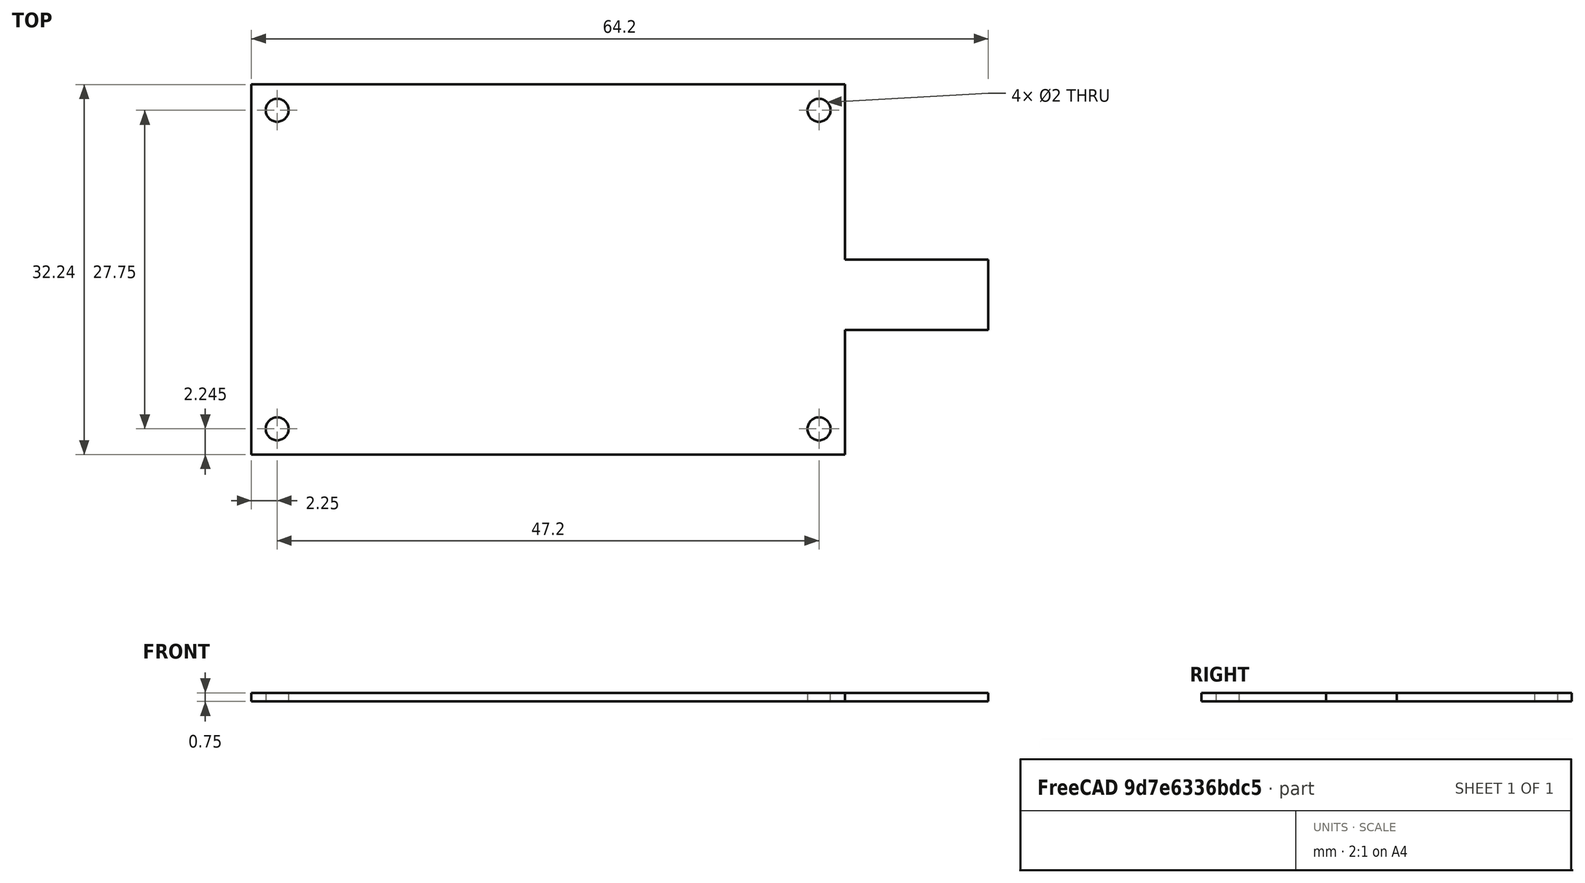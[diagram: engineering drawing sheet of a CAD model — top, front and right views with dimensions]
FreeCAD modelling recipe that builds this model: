
FCSTD DOCUMENT  (FreeCAD 1.0R39109 (Git))
Label: LightAPRS1
License: Creative Commons Attribution-ShareAlike 4.0
LicenseURL: https://creativecommons.org/licenses/by-sa/4.0/
objects: Sketcher::SketchObject×1, PartDesign::Pad×1, PartDesign::Body×1
note: 6 computed .brp shape members not serialized (recipe doc carries the construction recipe); baked Part::Feature solids carry a one-line shape summary decoded from their .brp

FEATURE [Sketcher::SketchObject] Sketch
  ArcFitTolerance = 1e-06
  AttachmentSupport = -> [XY_Plane]
  FullyConstrained = true
  MakeInternals = false
  MapMode = 5
  sketch-geometry (12):
    g0: LineSegment StartX=-25.85 StartY=16.125 StartZ=0 EndX=25.85 EndY=16.125 EndZ=0
    g1: LineSegment StartX=25.85 StartY=16.125 StartZ=0 EndX=25.85 EndY=0.875 EndZ=0
    g2: LineSegment StartX=25.85 StartY=0.875 StartZ=0 EndX=38.35 EndY=0.875 EndZ=0
    g3: LineSegment StartX=38.35 StartY=0.875 StartZ=0 EndX=38.35 EndY=-5.275 EndZ=0
    g4: LineSegment StartX=38.35 StartY=-5.275 StartZ=0 EndX=25.85 EndY=-5.275 EndZ=0
    g5: LineSegment StartX=25.85 StartY=-5.275 StartZ=0 EndX=25.85 EndY=-16.125 EndZ=0
    g6: LineSegment StartX=25.85 StartY=-16.125 StartZ=0 EndX=-25.85 EndY=-16.125 EndZ=0
    g7: LineSegment StartX=-25.85 StartY=-16.125 StartZ=0 EndX=-25.85 EndY=16.125 EndZ=0
    g8: Circle CenterX=-23.6 CenterY=13.875 CenterZ=0 NormalX=0 NormalY=0 NormalZ=1 AngleXU=0 Radius=1
    g9: Circle CenterX=23.6 CenterY=-13.875 CenterZ=0 NormalX=0 NormalY=0 NormalZ=1 AngleXU=0 Radius=1
    g10: Circle CenterX=23.6 CenterY=13.875 CenterZ=0 NormalX=0 NormalY=0 NormalZ=1 AngleXU=0 Radius=1
    g11: Circle CenterX=-23.6 CenterY=-13.875 CenterZ=0 NormalX=0 NormalY=0 NormalZ=1 AngleXU=0 Radius=1
  constraints (35):
    c: Horizontal(g0)
    c: Coincident(g0,g1)
    c: Vertical(g1)
    c: Coincident(g1,g2)
    c: Horizontal(g2)
    c: Coincident(g2,g3)
    c: Vertical(g3)
    c: Coincident(g3,g4)
    c: Horizontal(g4)
    c: Coincident(g4,g5)
    c: Vertical(g5)
    c: Coincident(g5,g6)
    c: Horizontal(g6)
    c: Coincident(g6,g7)
    c: Coincident(g7,g0)
    c: Vertical(g7)
    c: DistanceY(g6,g0) = 32.25
    c: Distance(g0,g1) = 51.7
    c: Vertical(g0,g5)
    c: Distance(g2,g3) = 6.15
    c: DistanceY(g1,g0) = 15.25
    c: Distance(g1,g2) = 12.5
    c: Symmetric(g0,g5,g-1)
    c: Diameter(g8) = 2
    c: Distance(g8,g7) = 2.25
    c: Distance(g8,g0) = 2.25
    c: Equal(g8,g10)
    c: Equal(g10,g9)
    c: Equal(g9,g11)
    c: Distance(g10,g1) = 2.25
    c: Distance(g10,g0) = 2.25
    c: Distance(g11,g7) = 2.25
    c: Distance(g11,g6) = 2.25
    c: Distance(g9,g5) = 2.25
    c: Distance(g9,g6) = 2.25
FEATURE [PartDesign::Pad] Pad  label="PCB"
  Direction = (0,0,1)
  Length = 0.75
  Length2 = 10
  Profile = -> Sketch
  ReferenceAxis = -> Sketch [N_Axis]
  Refine = true
  Suppressed = false
  Type = 0
FEATURE [PartDesign::Body] Body  label="PCB001"
  AllowCompound = false
  Group = -> [Sketch,Pad]
  Origin = -> Origin
  Tip = -> Pad
